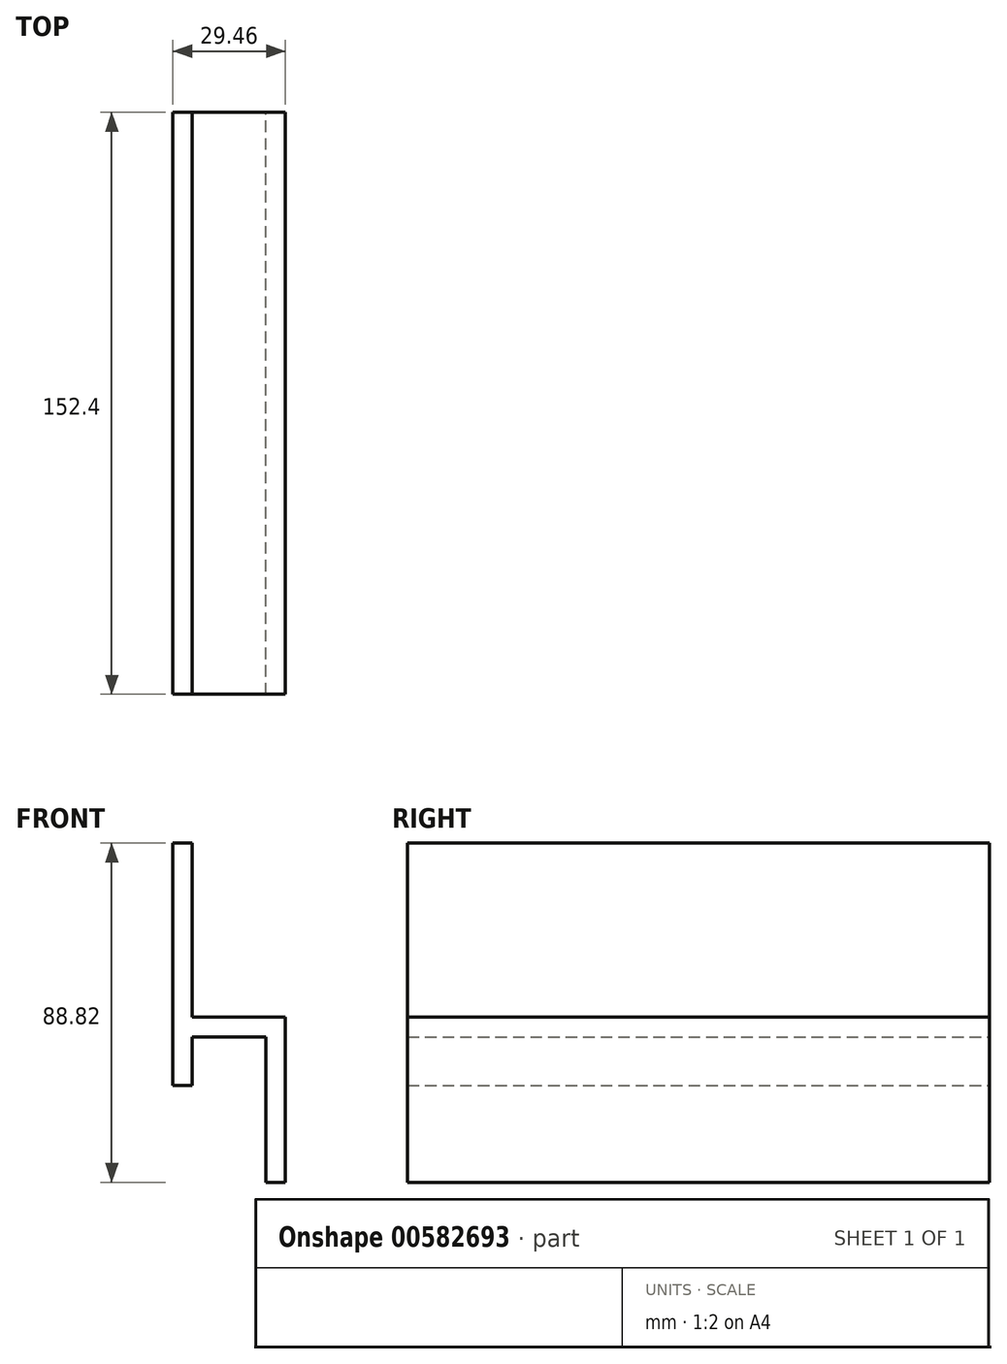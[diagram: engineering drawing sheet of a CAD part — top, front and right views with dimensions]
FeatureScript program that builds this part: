
annotation { "Feature Type Name" : "Feature", "Feature Type Description" : "" }
export const myFeature = defineFeature(function(context is Context, id is Id, definition is map)
    precondition{}
    {
        {
            var Q0;
            Q0=qCreatedBy(makeId("Right.planeOp"),FACE);
            var sketch = newSketch(context, id + "F0", { "sketchPlane" : qUnion([Q0])});
            skLineSegment(sketch, "E0.bottom", {"start": v(-76.2, 31.75) * mm, "end": v(76.2, 31.75) * mm});
            skLineSegment(sketch, "E0.top", {"start": v(-76.2, -31.75) * mm, "end": v(76.2, -31.75) * mm});
            skLineSegment(sketch, "E0.left", {"start": v(-76.2, 31.75) * mm, "end": v(-76.2, -31.75) * mm});
            skLineSegment(sketch, "E0.right", {"start": v(76.2, 31.75) * mm, "end": v(76.2, -31.75) * mm});
            skPoint(sketch, "E0.middle", {"position": v(0, 0) * mm});
            skSolve(sketch);
        }
        {
            var Q0;
            Q0 = qSketchRegion(id + "F0", true);
            extrude(context, id + "F1", {"entities" : qUnion([Q0]), "oppositeDirection" : true, "depth" : 5.08 * mm, "offsetDistance" : 25.4 * mm});
        }
        {
            var Q0;
            Q0=makeQuery(id+"F1.opExtrude","CAP_FACE",FACE,{"disambiguationData":[OSD([sQuery(id+"F0.wireOp",EDGE,"E0.bottom"),sQuery(id+"F0.wireOp",EDGE,"E0.top"),sQuery(id+"F0.wireOp",EDGE,"E0.left"),sQuery(id+"F0.wireOp",EDGE,"E0.right")])],"isStart":true});
            var sketch = newSketch(context, id + "F2", { "sketchPlane" : qUnion([Q0])});
            skSolve(sketch);
        }
        {
            var Q0;
            Q0=makeQuery(id+"F2.imprint","IMPRINT",FACE,{"disambiguationData":[TD([[makeQuery(id+"F2.imprint","IMPRINT",EDGE,{"derivedFrom":makeQuery(id+"F1.opExtrude","CAP_EDGE",EDGE,{"disambiguationData":[OSD([sQuery(id+"F0.wireOp",EDGE,"E0.bottom")])],"isStart":true})}),-1.0]])]});
            var sketch = newSketch(context, id + "F3", { "sketchPlane" : qUnion([Q0])});
            skLineSegment(sketch, "E1.bottom", {"start": v(-76.2, -18.97) * mm, "end": v(76.2, -18.97) * mm});
            skLineSegment(sketch, "E1.top", {"start": v(-76.2, -13.77) * mm, "end": v(76.2, -13.77) * mm});
            skLineSegment(sketch, "E1.left", {"start": v(-76.2, -18.97) * mm, "end": v(-76.2, -13.77) * mm});
            skLineSegment(sketch, "E1.right", {"start": v(76.2, -18.97) * mm, "end": v(76.2, -13.77) * mm});
            skSolve(sketch);
        }
        {
            var Q0;
            Q0 = qSketchRegion(id + "F3", true);
            extrude(context, id + "F4", {"entities" : qUnion([Q0]), "operationType" : NewBodyOperationType.ADD, "depth" : 24.38 * mm, "offsetDistance" : 25.4 * mm});
        }
        {
            var Q0;
            Q0=makeQuery(id+"F4.opExtrude","SWEPT_FACE",FACE,{"disambiguationData":[OSD([sQuery(id+"F3.wireOp",EDGE,"E1.bottom")])]});
            var sketch = newSketch(context, id + "F5", { "sketchPlane" : qUnion([Q0])});
            skLineSegment(sketch, "E2.bottom", {"start": v(24.38, 76.2) * mm, "end": v(19.3, 76.2) * mm});
            skLineSegment(sketch, "E2.top", {"start": v(24.38, -76.2) * mm, "end": v(19.3, -76.2) * mm});
            skLineSegment(sketch, "E2.left", {"start": v(24.38, 76.2) * mm, "end": v(24.38, -76.2) * mm});
            skLineSegment(sketch, "E2.right", {"start": v(19.3, 76.2) * mm, "end": v(19.3, -76.2) * mm});
            skSolve(sketch);
        }
        {
            var Q0;
            Q0 = qSketchRegion(id + "F5", true);
            extrude(context, id + "F6", {"entities" : qUnion([Q0]), "operationType" : NewBodyOperationType.ADD, "depth" : 38.1 * mm, "offsetDistance" : 25.4 * mm});
        }
    });
